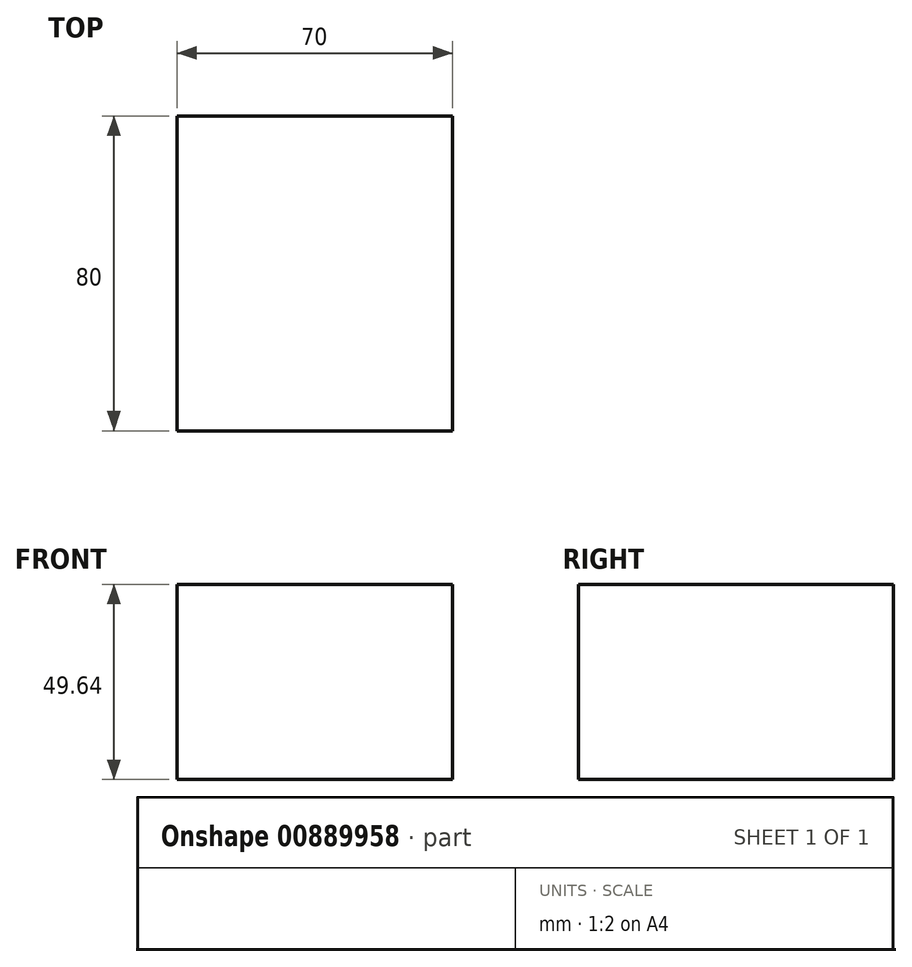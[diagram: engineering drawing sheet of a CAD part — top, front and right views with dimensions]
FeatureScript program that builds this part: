
annotation { "Feature Type Name" : "Feature", "Feature Type Description" : "" }
export const myFeature = defineFeature(function(context is Context, id is Id, definition is map)
    precondition{}
    {
        {
            var Q0;
            Q0=qCreatedBy(makeId("Right.planeOp"),FACE);
            var sketch = newSketch(context, id + "F0", { "sketchPlane" : qUnion([Q0])});
            skLineSegment(sketch, "E0", {"start": v(0, 0) * mm, "end": v(0, 600) * mm});
            skLineSegment(sketch, "E1", {"start": v(0, 0) * mm, "end": v(40, 0) * mm});
            skLineSegment(sketch, "E2", {"start": v(40, 0) * mm, "end": v(-40, 0) * mm});
            skLineSegment(sketch, "E3", {"start": v(-40, 0) * mm, "end": v(-40, 600) * mm});
            skLineSegment(sketch, "E4", {"start": v(-40, 600) * mm, "end": v(40, 600) * mm});
            skLineSegment(sketch, "E5", {"start": v(40, 600) * mm, "end": v(40, 0) * mm});
            skCircle(sketch, "E6", {"center": v(0, 566.23) * mm, "radius": 25 * mm});
            skLineSegment(sketch, "E7", {"start": v(-40, 600) * mm, "end": v(-40, 535) * mm});
            skLineSegment(sketch, "E8", {"start": v(-40, 535) * mm, "end": v(40, 535) * mm});
            skLineSegment(sketch, "E9", {"start": v(40, 535) * mm, "end": v(40, 600) * mm});
            skLineSegment(sketch, "E10", {"start": v(-40, 0) * mm, "end": v(-390, 0) * mm});
            skLineSegment(sketch, "E11", {"start": v(-390, 0) * mm, "end": v(-40, 600) * mm});
            skLineSegment(sketch, "E12", {"start": v(-40, 535) * mm, "end": v(-352.08, 0) * mm});
            skLineSegment(sketch, "E13", {"start": v(40, 0) * mm, "end": v(390, 0) * mm});
            skLineSegment(sketch, "E14", {"start": v(390, 0) * mm, "end": v(40, 600) * mm});
            skLineSegment(sketch, "E15", {"start": v(40, 535) * mm, "end": v(352.08, 0) * mm});
            skLineSegment(sketch, "E16", {"start": v(-352.08, 0) * mm, "end": v(-196.04, 267.5) * mm});
            skLineSegment(sketch, "E17", {"start": v(-196.04, 267.5) * mm, "end": v(196.04, 267.5) * mm});
            skLineSegment(sketch, "E18", {"start": v(196.04, 267.5) * mm, "end": v(167.08, 317.14) * mm});
            skLineSegment(sketch, "E19", {"start": v(167.08, 317.14) * mm, "end": v(-167.08, 317.14) * mm});
            skLineSegment(sketch, "E20", {"start": v(-167.08, 317.14) * mm, "end": v(-196.04, 267.5) * mm});
            skSolve(sketch);
        }
        {
            var Q0;
            Q0=makeQuery(id+"F0.imprint","IMPRINT",FACE,{"disambiguationData":[TD([[makeQuery(id+"F0.imprint","IMPRINT",EDGE,{"derivedFrom":sQuery(id+"F0.wireOp",EDGE,"E7")}),-1.0]])]});
            var Q1;
            {var subQ6=sQuery(id+"F0.wireOp",EDGE,"E9");Q1=makeQuery(id+"F0.imprint","IMPRINT",FACE,{"disambiguationData":[TD([[makeQuery(id+"F0.imprint","IMPRINT",EDGE,{"derivedFrom":subQ6}),1.0]])]});}
            var Q2;
            {var subQ6=sQuery(id+"F0.wireOp",EDGE,"E7");Q2=makeQuery(id+"F0.imprint","IMPRINT",FACE,{"disambiguationData":[TD([[makeQuery(id+"F0.imprint","IMPRINT",EDGE,{"derivedFrom":subQ6}),1.0]])]});}
            var Q3;
            {var subQ1=sQuery(id+"F0.wireOp",EDGE,"E9");Q3=makeQuery(id+"F0.imprint","IMPRINT",FACE,{"disambiguationData":[TD([[makeQuery(id+"F0.imprint","IMPRINT",EDGE,{"derivedFrom":subQ1}),-1.0]])]});}
            var Q4;
            {var subQ5=sQuery(id+"F0.wireOp",EDGE,"E18");Q4=makeQuery(id+"F0.imprint","IMPRINT",FACE,{"disambiguationData":[TD([[makeQuery(id+"F0.imprint","IMPRINT",EDGE,{"derivedFrom":subQ5}),1.0]])]});}
            var Q5;
            {var subQ0=sQuery(id+"F0.wireOp",EDGE,"E17");var subQ1=sQuery(id+"F0.wireOp",EDGE,"E0");var subQ2=makeQuery(id+"F0.imprint","INTERSECT",VERTEX,{"derivedFrom":[subQ1,subQ0]});Q5=makeQuery(id+"F0.imprint","IMPRINT",FACE,{"disambiguationData":[TD([[makeQuery(id+"F0.imprint","IMPRINT",EDGE,{"disambiguationData":[TD([[subQ2,-1.0]])],"derivedFrom":subQ1}),-1.0]])]});}
            var Q6;
            {var subQ0=sQuery(id+"F0.wireOp",EDGE,"E17");var subQ1=sQuery(id+"F0.wireOp",EDGE,"E0");var subQ2=makeQuery(id+"F0.imprint","INTERSECT",VERTEX,{"derivedFrom":[subQ1,subQ0]});Q6=makeQuery(id+"F0.imprint","IMPRINT",FACE,{"disambiguationData":[TD([[makeQuery(id+"F0.imprint","IMPRINT",EDGE,{"disambiguationData":[TD([[subQ2,-1.0]])],"derivedFrom":subQ1}),1.0]])]});}
            var Q7;
            {var subQ5=sQuery(id+"F0.wireOp",EDGE,"E20");Q7=makeQuery(id+"F0.imprint","IMPRINT",FACE,{"disambiguationData":[TD([[makeQuery(id+"F0.imprint","IMPRINT",EDGE,{"derivedFrom":subQ5}),1.0]])]});}
            extrude(context, id + "F1", {"entities" : qUnion([Q0, Q1, Q2, Q3, Q4, Q5, Q6, Q7]), "depth" : 70 * mm, "offsetDistance" : 25 * mm});
        }
    });
